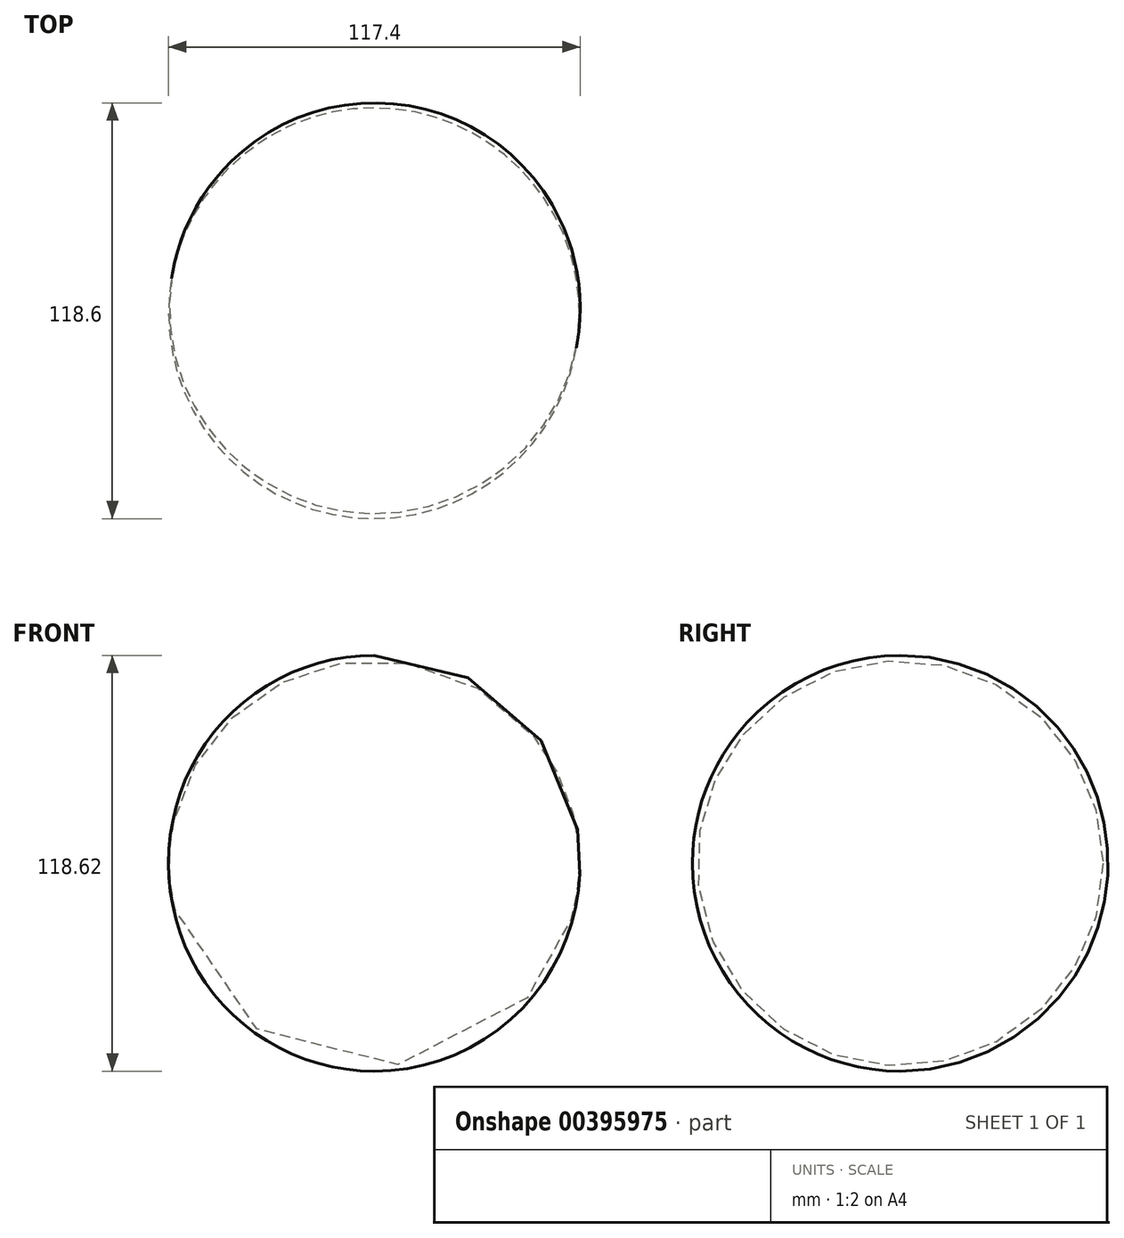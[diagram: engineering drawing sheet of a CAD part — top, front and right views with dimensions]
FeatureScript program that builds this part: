
annotation { "Feature Type Name" : "Feature", "Feature Type Description" : "" }
export const myFeature = defineFeature(function(context is Context, id is Id, definition is map)
    precondition{}
    {
        {
            var Q0;
            Q0=qCreatedBy(makeId("Top.planeOp"),FACE);
            var sketch = newSketch(context, id + "F0", { "sketchPlane" : qUnion([Q0])});
            skCircle(sketch, "E0", {"center": v(-52.07, 23.36) * mm, "radius": 58.58 * mm});
            skLineSegment(sketch, "E1", {"start": v(-109.67, 33.97) * mm, "end": v(5.79, 14.2) * mm});
            skSolve(sketch);
        }
        {
            var Q0;
            {var subQ0=sQuery(id+"F0.wireOp",EDGE,"E1");Q0=makeQuery(id+"F0.imprint","IMPRINT",FACE,{"disambiguationData":[TD([[makeQuery(id+"F0.imprint","IMPRINT",EDGE,{"derivedFrom":subQ0}),-1.0]])]});}
            var Q1;
            Q1=sQuery(id+"F0.wireOp",EDGE,"E1");
            revolve(context, id + "F1", {"entities" : qUnion([Q0]), "axis" : qUnion([Q1]), "revolveType" : RevolveType.FULL});
        }
    });
